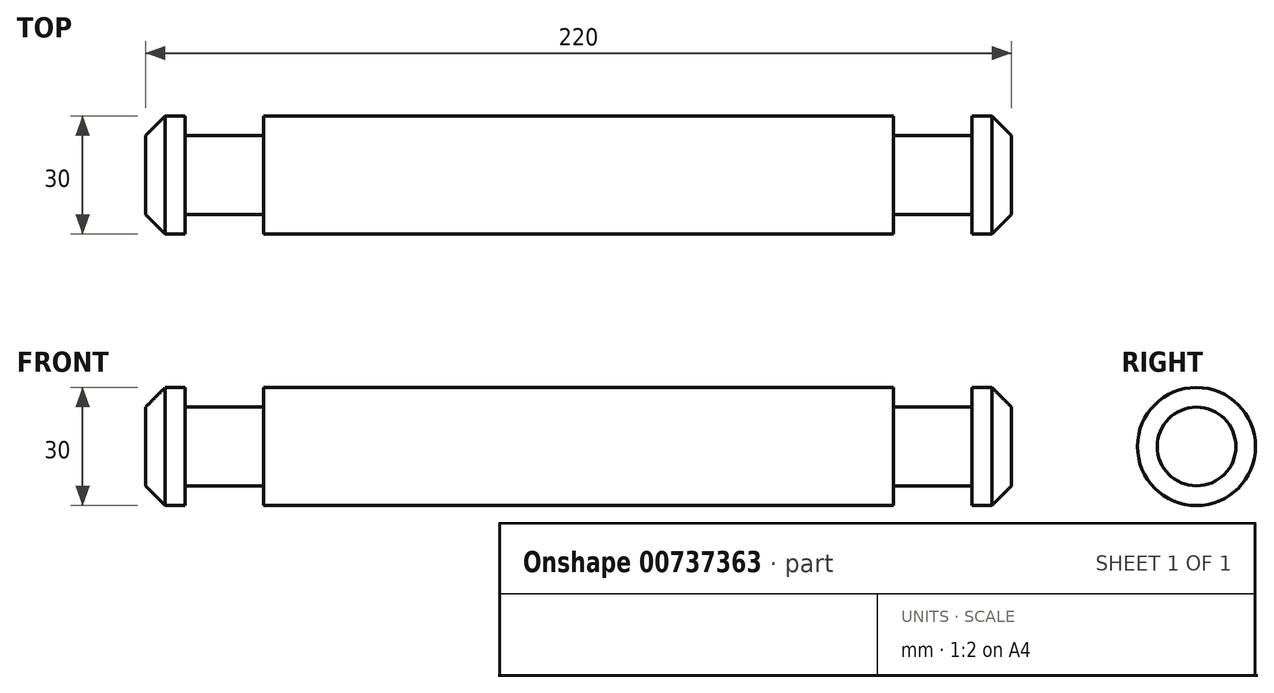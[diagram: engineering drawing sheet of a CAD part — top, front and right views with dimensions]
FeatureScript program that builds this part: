
annotation { "Feature Type Name" : "Feature", "Feature Type Description" : "" }
export const myFeature = defineFeature(function(context is Context, id is Id, definition is map)
    precondition{}
    {
        {
            var Q0;
            Q0=qCreatedBy(makeId("Front.planeOp"), FACE);
            var sketch = newSketch(context, id + "F0", { "sketchPlane" : qUnion([Q0])});
            skLineSegment(sketch, "E0", {"start": v(0, 0) * mm, "end": v(110, 0) * mm});
            skLineSegment(sketch, "E1", {"start": v(110, 0) * mm, "end": v(110, 10) * mm});
            skLineSegment(sketch, "E2", {"start": v(110, 10) * mm, "end": v(105, 15) * mm});
            skLineSegment(sketch, "E3", {"start": v(105, 15) * mm, "end": v(100, 15) * mm});
            skLineSegment(sketch, "E4", {"start": v(100, 15) * mm, "end": v(100, 10) * mm});
            skLineSegment(sketch, "E5", {"start": v(100, 10) * mm, "end": v(80, 10) * mm});
            skLineSegment(sketch, "E6", {"start": v(80, 10) * mm, "end": v(80, 15) * mm});
            skLineSegment(sketch, "E7", {"start": v(80, 15) * mm, "end": v(-80, 15) * mm});
            skLineSegment(sketch, "E8", {"start": v(-80, 15) * mm, "end": v(-80, 10) * mm});
            skLineSegment(sketch, "E9", {"start": v(-80, 10) * mm, "end": v(-100, 10) * mm});
            skLineSegment(sketch, "E10", {"start": v(-100, 10) * mm, "end": v(-100, 15) * mm});
            skLineSegment(sketch, "E11", {"start": v(-100, 15) * mm, "end": v(-105, 15) * mm});
            skLineSegment(sketch, "E12", {"start": v(-105, 15) * mm, "end": v(-110, 10) * mm});
            skLineSegment(sketch, "E13", {"start": v(-110, 10) * mm, "end": v(-110, 0) * mm});
            skLineSegment(sketch, "E14", {"start": v(-110, 0) * mm, "end": v(0, 0) * mm});
            skSolve(sketch);
        }
        {
            var Q0;
            Q0=makeQuery(id+"F0.imprint","IMPRINT",FACE,{"disambiguationData":[TD([[makeQuery(id+"F0.imprint","IMPRINT",EDGE,{"derivedFrom":sQuery(id+"F0.wireOp",EDGE,"E0")}),1.0]])]});
            var Q1;
            Q1=sQuery(id+"F0.wireOp",EDGE,"E14");
            revolve(context, id + "F1", {"surfaceOperationType" : NewSurfaceOperationType.NEW, "entities" : qUnion([Q0]), "axis" : qUnion([Q1]), "revolveType" : RevolveType.FULL});
        }
    });
